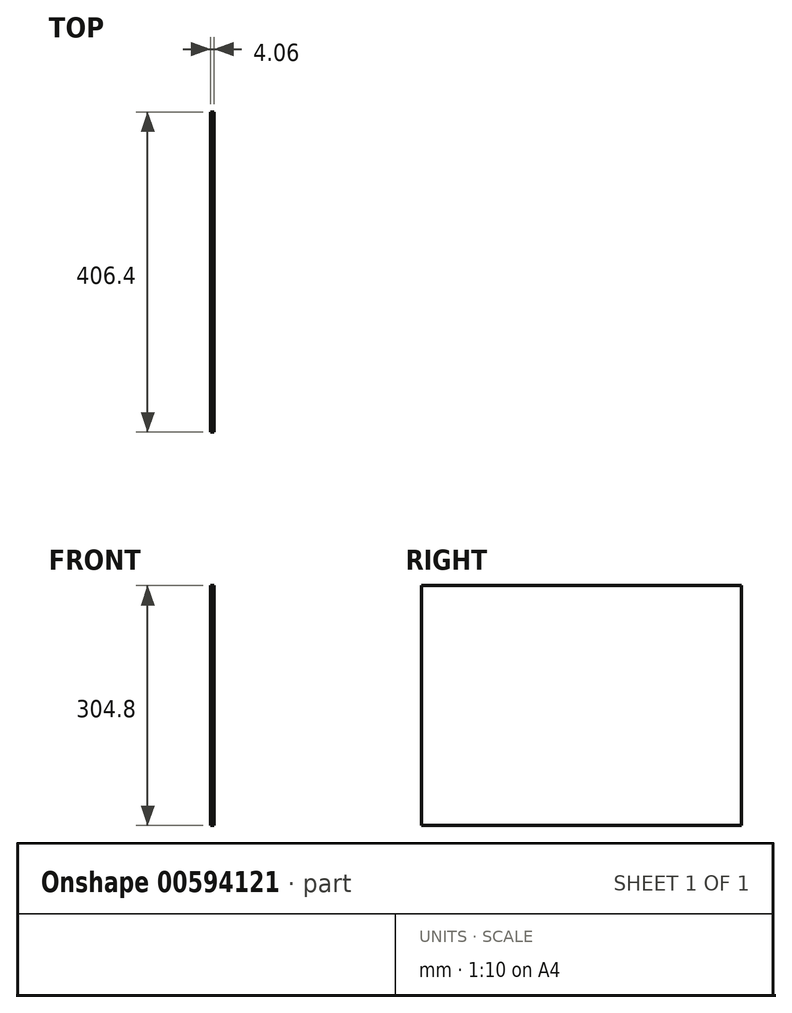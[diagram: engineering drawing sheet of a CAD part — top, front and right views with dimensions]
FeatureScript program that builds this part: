
annotation { "Feature Type Name" : "Feature", "Feature Type Description" : "" }
export const myFeature = defineFeature(function(context is Context, id is Id, definition is map)
    precondition{}
    {
        {
            var Q0;
            Q0=qCreatedBy(makeId("Right.planeOp"),FACE);
            var sketch = newSketch(context, id + "F0", { "sketchPlane" : qUnion([Q0])});
            skLineSegment(sketch, "E0.bottom", {"start": v(-203.2, -152.4) * mm, "end": v(203.2, -152.4) * mm});
            skLineSegment(sketch, "E0.top", {"start": v(-203.2, 152.4) * mm, "end": v(203.2, 152.4) * mm});
            skLineSegment(sketch, "E0.left", {"start": v(-203.2, -152.4) * mm, "end": v(-203.2, 152.4) * mm});
            skLineSegment(sketch, "E0.right", {"start": v(203.2, -152.4) * mm, "end": v(203.2, 152.4) * mm});
            skPoint(sketch, "E0.middle", {"position": v(0, 0) * mm});
            skSolve(sketch);
        }
        {
            var Q0;
            Q0 = qSketchRegion(id + "F0", true);
            extrude(context, id + "F1", {"entities" : qUnion([Q0]), "depth" : 4.06 * mm, "offsetDistance" : 25.4 * mm});
        }
    });
